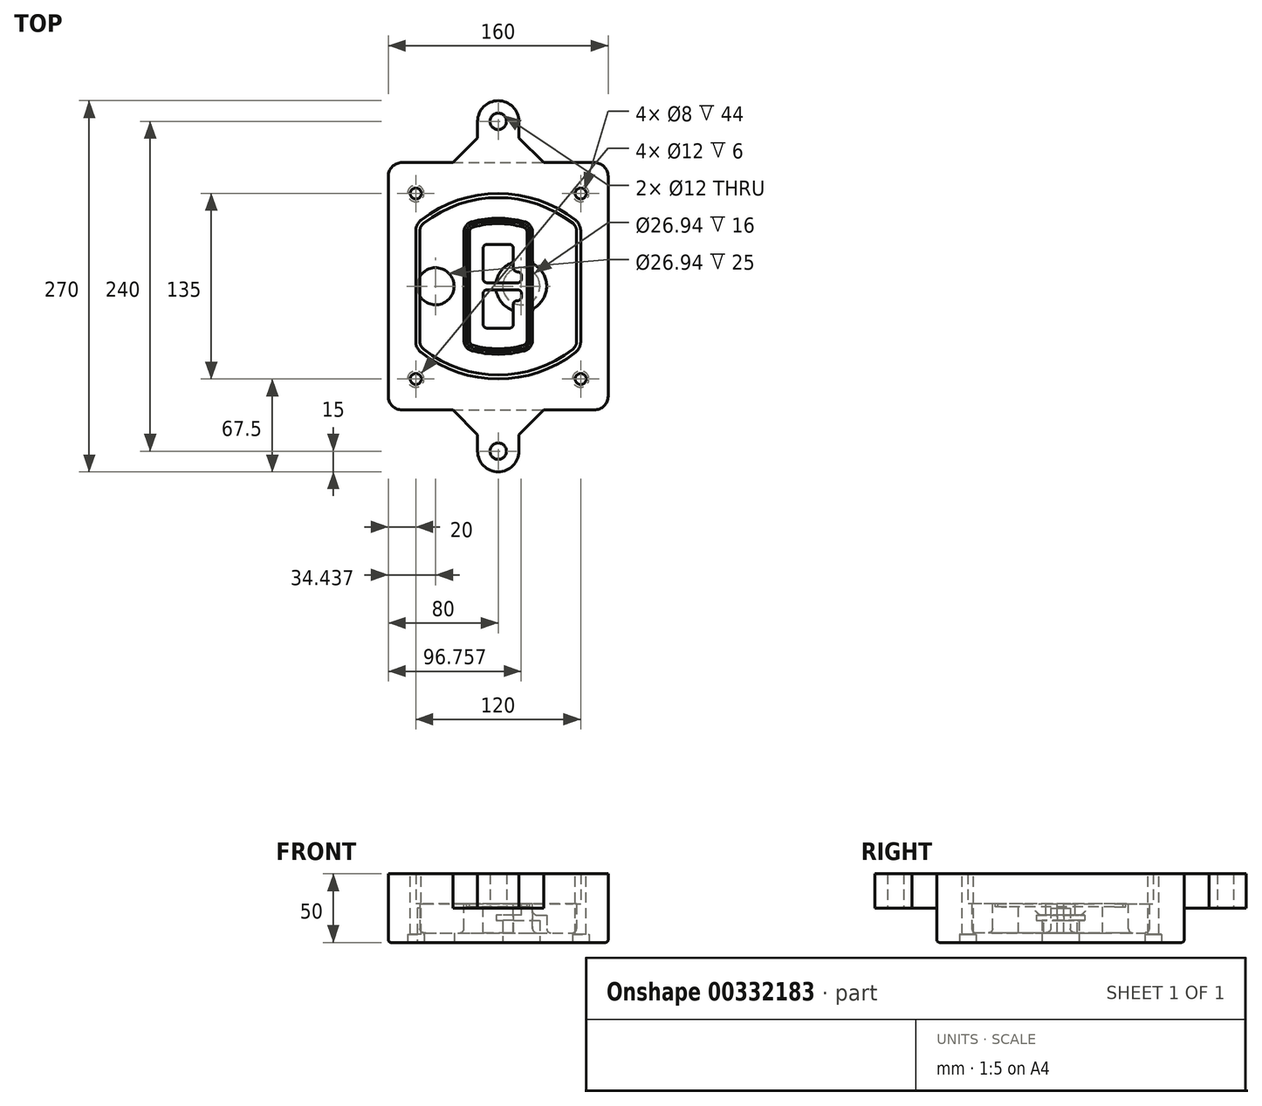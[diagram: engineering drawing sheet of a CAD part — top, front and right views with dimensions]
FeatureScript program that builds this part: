
annotation { "Feature Type Name" : "Feature", "Feature Type Description" : "" }
export const myFeature = defineFeature(function(context is Context, id is Id, definition is map)
    precondition{}
    {
        {
            var Q0;
            Q0=qCreatedBy(makeId("Top.planeOp"),FACE);
            var sketch = newSketch(context, id + "F0", { "sketchPlane" : qUnion([Q0])});
            skPoint(sketch, "E0.rect.middle", {"position": v(0, 0) * mm});
            skLineSegment(sketch, "E1.bottom", {"start": v(-70, -90) * mm, "end": v(70, -90) * mm});
            skLineSegment(sketch, "E1.top", {"start": v(-70, 90) * mm, "end": v(70, 90) * mm});
            skLineSegment(sketch, "E1.left", {"start": v(-80, -80) * mm, "end": v(-80, 80) * mm});
            skLineSegment(sketch, "E1.right", {"start": v(80, -80) * mm, "end": v(80, 80) * mm});
            skLineSegment(sketch, "E2", {"start": v(-80, 90) * mm, "end": v(80, -90) * mm, "construction": true});
            skLineSegment(sketch, "E3", {"start": v(80, 90) * mm, "end": v(-80, -90) * mm, "construction": true});
            skCircle(sketch, "E4", {"center": v(-60, 67.5) * mm, "radius": 4 * mm});
            skCircle(sketch, "E5", {"center": v(60, 67.5) * mm, "radius": 4 * mm});
            skCircle(sketch, "E6", {"center": v(60, -67.5) * mm, "radius": 4 * mm});
            skCircle(sketch, "E7", {"center": v(-60, -67.5) * mm, "radius": 4 * mm});
            skLineSegment(sketch, "E8", {"start": v(-60, 67.5) * mm, "end": v(60, 67.5) * mm, "construction": true});
            skLineSegment(sketch, "E9", {"start": v(60, 67.5) * mm, "end": v(60, -67.5) * mm, "construction": true});
            skLineSegment(sketch, "E10", {"start": v(60, -67.5) * mm, "end": v(-60, -67.5) * mm, "construction": true});
            skLineSegment(sketch, "E11", {"start": v(-60, -67.5) * mm, "end": v(-60, 67.5) * mm, "construction": true});
            skLineSegment(sketch, "E12", {"start": v(-60, 40.3) * mm, "end": v(-60, -40.3) * mm});
            skLineSegment(sketch, "E13", {"start": v(60, 40.3) * mm, "end": v(60, -40.3) * mm});
            skArc(sketch, "E14", {"start": v(56.15, 48.18) * mm, "mid": v(0, 67.5) * mm, "end": v(-56.15, 48.18) * mm});
            skArc(sketch, "E15", {"start": v(-56.15, -48.18) * mm, "mid": v(0, -67.5) * mm, "end": v(56.15, -48.18) * mm});
            skLineSegment(sketch, "E16", {"start": v(-60, 0) * mm, "end": v(60, 0) * mm, "construction": true});
            skPoint(sketch, "E17.visualSharp", {"position": v(-60, -45) * mm});
            skArc(sketch, "E17.filletArc", {"start": v(-60, -40.3) * mm, "mid": v(-58.99, -44.68) * mm, "end": v(-56.15, -48.18) * mm});
            skPoint(sketch, "E18.visualSharp", {"position": v(-60, 45) * mm});
            skArc(sketch, "E18.filletArc", {"start": v(-56.15, 48.18) * mm, "mid": v(-58.99, 44.68) * mm, "end": v(-60, 40.3) * mm});
            skPoint(sketch, "E19.visualSharp", {"position": v(60, 45) * mm});
            skArc(sketch, "E19.filletArc", {"start": v(60, 40.3) * mm, "mid": v(58.99, 44.68) * mm, "end": v(56.15, 48.18) * mm});
            skPoint(sketch, "E20.visualSharp", {"position": v(60, -45) * mm});
            skArc(sketch, "E20.filletArc", {"start": v(56.15, -48.18) * mm, "mid": v(58.99, -44.68) * mm, "end": v(60, -40.3) * mm});
            skPoint(sketch, "E21.visualSharp", {"position": v(-80, 90) * mm});
            skArc(sketch, "E21.filletArc", {"start": v(-70, 90) * mm, "mid": v(-77.07, 87.07) * mm, "end": v(-80, 80) * mm});
            skPoint(sketch, "E22.visualSharp", {"position": v(80, 90) * mm});
            skArc(sketch, "E22.filletArc", {"start": v(80, 80) * mm, "mid": v(77.07, 87.07) * mm, "end": v(70, 90) * mm});
            skPoint(sketch, "E23.visualSharp", {"position": v(80, -90) * mm});
            skArc(sketch, "E23.filletArc", {"start": v(70, -90) * mm, "mid": v(77.07, -87.07) * mm, "end": v(80, -80) * mm});
            skPoint(sketch, "E24.visualSharp", {"position": v(-80, -90) * mm});
            skArc(sketch, "E24.filletArc", {"start": v(-80, -80) * mm, "mid": v(-77.07, -87.07) * mm, "end": v(-70, -90) * mm});
            skArc(sketch, "E25.0", {"start": v(57, 40.3) * mm, "mid": v(56.3, 43.36) * mm, "end": v(54.3, 45.81) * mm});
            skLineSegment(sketch, "E25.1", {"start": v(57, 40.3) * mm, "end": v(57, -40.3) * mm});
            skArc(sketch, "E25.2", {"start": v(54.3, -45.81) * mm, "mid": v(56.3, -43.36) * mm, "end": v(57, -40.3) * mm});
            skArc(sketch, "E25.3", {"start": v(-54.3, -45.81) * mm, "mid": v(0, -64.5) * mm, "end": v(54.3, -45.81) * mm});
            skArc(sketch, "E25.4", {"start": v(-57, -40.3) * mm, "mid": v(-56.3, -43.36) * mm, "end": v(-54.3, -45.81) * mm});
            skArc(sketch, "E25.5", {"start": v(54.3, 45.81) * mm, "mid": v(0, 64.5) * mm, "end": v(-54.3, 45.81) * mm});
            skLineSegment(sketch, "E25.6", {"start": v(-57, 40.3) * mm, "end": v(-57, -40.3) * mm});
            skArc(sketch, "E25.7", {"start": v(-54.3, 45.81) * mm, "mid": v(-56.3, 43.36) * mm, "end": v(-57, 40.3) * mm});
            skArc(sketch, "E26.0", {"start": v(-58.62, 51.33) * mm, "mid": v(-62.58, 46.43) * mm, "end": v(-64, 40.3) * mm});
            skArc(sketch, "E26.1", {"start": v(58.62, 51.33) * mm, "mid": v(0, 71.5) * mm, "end": v(-58.62, 51.33) * mm});
            skArc(sketch, "E26.2", {"start": v(64, 40.3) * mm, "mid": v(62.58, 46.43) * mm, "end": v(58.62, 51.33) * mm});
            skLineSegment(sketch, "E26.3", {"start": v(64, 40.3) * mm, "end": v(64, -40.3) * mm});
            skArc(sketch, "E26.4", {"start": v(58.62, -51.33) * mm, "mid": v(62.58, -46.43) * mm, "end": v(64, -40.3) * mm});
            skLineSegment(sketch, "E26.5", {"start": v(-64, 40.3) * mm, "end": v(-64, -40.3) * mm});
            skArc(sketch, "E26.6", {"start": v(-58.62, -51.33) * mm, "mid": v(0, -71.5) * mm, "end": v(58.62, -51.33) * mm});
            skArc(sketch, "E26.7", {"start": v(-64, -40.3) * mm, "mid": v(-62.58, -46.43) * mm, "end": v(-58.62, -51.33) * mm});
            skSolve(sketch);
        }
        {
            var Q0;
            Q0=makeQuery(id+"F0.imprint","IMPRINT",FACE,{"disambiguationData":[TD([[makeQuery(id+"F0.imprint","IMPRINT",EDGE,{"derivedFrom":sQuery(id+"F0.wireOp",EDGE,"E1.bottom")}),1.0]])]});
            var Q1;
            Q1=makeQuery(id+"F0.imprint","IMPRINT",FACE,{"disambiguationData":[TD([[makeQuery(id+"F0.imprint","IMPRINT",EDGE,{"derivedFrom":sQuery(id+"F0.wireOp",EDGE,"E12")}),1.0]])]});
            var Q2;
            Q2=makeQuery(id+"F0.imprint","IMPRINT",FACE,{"disambiguationData":[TD([[makeQuery(id+"F0.imprint","IMPRINT",EDGE,{"derivedFrom":sQuery(id+"F0.wireOp",EDGE,"E25.0")}),1.0]])]});
            var Q3;
            Q3=makeQuery(id+"F0.imprint","IMPRINT",FACE,{"disambiguationData":[TD([[makeQuery(id+"F0.imprint","IMPRINT",EDGE,{"derivedFrom":sQuery(id+"F0.wireOp",EDGE,"E12")}),-1.0]])]});
            extrude(context, id + "F1", {"entities" : qUnion([Q0, Q1, Q2, Q3]), "oppositeDirection" : true, "depth" : 25 * mm});
        }
        {
            var Q0;
            Q0=makeQuery(id+"F0.imprint","IMPRINT",FACE,{"disambiguationData":[TD([[makeQuery(id+"F0.imprint","IMPRINT",EDGE,{"derivedFrom":sQuery(id+"F0.wireOp",EDGE,"E12")}),1.0]])]});
            extrude(context, id + "F2", {"entities" : qUnion([Q0]), "operationType" : NewBodyOperationType.ADD, "depth" : 3 * mm});
        }
        {
            var Q0;
            Q0=makeQuery(id+"F0.imprint","IMPRINT",FACE,{"disambiguationData":[TD([[makeQuery(id+"F0.imprint","IMPRINT",EDGE,{"derivedFrom":sQuery(id+"F0.wireOp",EDGE,"E25.0")}),1.0]])]});
            extrude(context, id + "F3", {"entities" : qUnion([Q0]), "operationType" : NewBodyOperationType.REMOVE, "oppositeDirection" : true, "depth" : 18 * mm});
        }
        {
            var Q0;
            Q0=makeQuery(id+"F2.opExtrude","CAP_FACE",FACE,{"disambiguationData":[OSD([sQuery(id+"F0.wireOp",EDGE,"E12"),sQuery(id+"F0.wireOp",EDGE,"E13"),sQuery(id+"F0.wireOp",EDGE,"E14"),sQuery(id+"F0.wireOp",EDGE,"E15"),sQuery(id+"F0.wireOp",EDGE,"E17.filletArc"),sQuery(id+"F0.wireOp",EDGE,"E18.filletArc"),sQuery(id+"F0.wireOp",EDGE,"E19.filletArc"),sQuery(id+"F0.wireOp",EDGE,"E20.filletArc"),sQuery(id+"F0.wireOp",EDGE,"E25.0"),sQuery(id+"F0.wireOp",EDGE,"E25.1"),sQuery(id+"F0.wireOp",EDGE,"E25.2"),sQuery(id+"F0.wireOp",EDGE,"E25.3"),sQuery(id+"F0.wireOp",EDGE,"E25.4"),sQuery(id+"F0.wireOp",EDGE,"E25.5"),sQuery(id+"F0.wireOp",EDGE,"E25.6"),sQuery(id+"F0.wireOp",EDGE,"E25.7")])],"isStart":false});
            var sketch = newSketch(context, id + "F4", { "sketchPlane" : qUnion([Q0])});
            skArc(sketch, "E27.0", {"start": v(-19.08, -46.97) * mm, "mid": v(0, -49.5) * mm, "end": v(19.08, -46.97) * mm});
            skArc(sketch, "E28.0", {"start": v(19.08, 46.97) * mm, "mid": v(0, 49.5) * mm, "end": v(-19.08, 46.97) * mm});
            skLineSegment(sketch, "E29", {"start": v(-25, 39.25) * mm, "end": v(-25, -39.25) * mm});
            skLineSegment(sketch, "E30", {"start": v(25, 39.25) * mm, "end": v(25, -39.25) * mm});
            skLineSegment(sketch, "E31", {"start": v(-25, 45.1) * mm, "end": v(25, 45.1) * mm, "construction": true});
            skLineSegment(sketch, "E32", {"start": v(-25, -45.1) * mm, "end": v(25, -45.1) * mm, "construction": true});
            skPoint(sketch, "E33.visualSharp", {"position": v(-25, 45.1) * mm});
            skArc(sketch, "E33.filletArc", {"start": v(-19.08, 46.97) * mm, "mid": v(-23.35, 44.11) * mm, "end": v(-25, 39.25) * mm});
            skPoint(sketch, "E34.visualSharp", {"position": v(25, 45.1) * mm});
            skArc(sketch, "E34.filletArc", {"start": v(25, 39.25) * mm, "mid": v(23.35, 44.11) * mm, "end": v(19.08, 46.97) * mm});
            skPoint(sketch, "E35.visualSharp", {"position": v(25, -45.1) * mm});
            skArc(sketch, "E35.filletArc", {"start": v(19.08, -46.97) * mm, "mid": v(23.35, -44.11) * mm, "end": v(25, -39.25) * mm});
            skPoint(sketch, "E36.visualSharp", {"position": v(-25, -45.1) * mm});
            skArc(sketch, "E36.filletArc", {"start": v(-25, -39.25) * mm, "mid": v(-23.35, -44.11) * mm, "end": v(-19.08, -46.97) * mm});
            skArc(sketch, "E37.0", {"start": v(54.3, 45.81) * mm, "mid": v(0, 64.5) * mm, "end": v(-54.3, 45.81) * mm});
            skArc(sketch, "E37.1", {"start": v(-54.3, 45.81) * mm, "mid": v(-56.3, 43.36) * mm, "end": v(-57, 40.3) * mm});
            skLineSegment(sketch, "E37.2", {"start": v(-57, 40.3) * mm, "end": v(-57, -40.3) * mm});
            skArc(sketch, "E37.3", {"start": v(-57, -40.3) * mm, "mid": v(-56.3, -43.36) * mm, "end": v(-54.3, -45.81) * mm});
            skArc(sketch, "E37.4", {"start": v(-54.3, -45.81) * mm, "mid": v(0, -64.5) * mm, "end": v(54.3, -45.81) * mm});
            skArc(sketch, "E37.5", {"start": v(54.3, -45.81) * mm, "mid": v(56.3, -43.36) * mm, "end": v(57, -40.3) * mm});
            skLineSegment(sketch, "E37.6", {"start": v(57, 40.3) * mm, "end": v(57, -40.3) * mm});
            skArc(sketch, "E37.7", {"start": v(57, 40.3) * mm, "mid": v(56.3, 43.36) * mm, "end": v(54.3, 45.81) * mm});
            skLineSegment(sketch, "E38.0", {"start": v(23, 39.25) * mm, "end": v(23, -39.25) * mm});
            skArc(sketch, "E38.1", {"start": v(18.56, -45.04) * mm, "mid": v(21.76, -42.9) * mm, "end": v(23, -39.25) * mm});
            skArc(sketch, "E38.2", {"start": v(-18.56, -45.04) * mm, "mid": v(0, -47.5) * mm, "end": v(18.56, -45.04) * mm});
            skArc(sketch, "E38.3", {"start": v(-23, -39.25) * mm, "mid": v(-21.76, -42.9) * mm, "end": v(-18.56, -45.04) * mm});
            skLineSegment(sketch, "E38.4", {"start": v(-23, 39.25) * mm, "end": v(-23, -39.25) * mm});
            skArc(sketch, "E38.5", {"start": v(23, 39.25) * mm, "mid": v(21.76, 42.9) * mm, "end": v(18.56, 45.04) * mm});
            skArc(sketch, "E38.6", {"start": v(-18.56, 45.04) * mm, "mid": v(-21.76, 42.9) * mm, "end": v(-23, 39.25) * mm});
            skArc(sketch, "E38.7", {"start": v(18.56, 45.04) * mm, "mid": v(0, 47.5) * mm, "end": v(-18.56, 45.04) * mm});
            skArc(sketch, "E39.0", {"start": v(21, 39.25) * mm, "mid": v(20.18, 41.68) * mm, "end": v(18.04, 43.1) * mm});
            skLineSegment(sketch, "E39.1", {"start": v(21, 39.25) * mm, "end": v(21, -39.25) * mm});
            skArc(sketch, "E39.2", {"start": v(18.04, -43.1) * mm, "mid": v(20.18, -41.68) * mm, "end": v(21, -39.25) * mm});
            skArc(sketch, "E39.3", {"start": v(-18.04, -43.1) * mm, "mid": v(0, -45.5) * mm, "end": v(18.04, -43.1) * mm});
            skArc(sketch, "E39.4", {"start": v(-21, -39.25) * mm, "mid": v(-20.18, -41.68) * mm, "end": v(-18.04, -43.1) * mm});
            skArc(sketch, "E39.5", {"start": v(18.04, 43.1) * mm, "mid": v(0, 45.5) * mm, "end": v(-18.04, 43.1) * mm});
            skLineSegment(sketch, "E39.6", {"start": v(-21, 39.25) * mm, "end": v(-21, -39.25) * mm});
            skArc(sketch, "E39.7", {"start": v(-18.04, 43.1) * mm, "mid": v(-20.18, 41.68) * mm, "end": v(-21, 39.25) * mm});
            skLineSegment(sketch, "E40", {"start": v(-25, 0) * mm, "end": v(25, 0) * mm, "construction": true});
            skLineSegment(sketch, "E41", {"start": v(-11, 5.5) * mm, "end": v(-11, 27.5) * mm});
            skLineSegment(sketch, "E42", {"start": v(-8, 30.5) * mm, "end": v(8, 30.5) * mm});
            skLineSegment(sketch, "E43", {"start": v(11, 27.5) * mm, "end": v(11, 13.5) * mm});
            skLineSegment(sketch, "E44", {"start": v(14, 10.5) * mm, "end": v(14, 10.5) * mm});
            skLineSegment(sketch, "E45", {"start": v(17, 7.5) * mm, "end": v(17, 5.5) * mm});
            skLineSegment(sketch, "E46", {"start": v(14, 2.5) * mm, "end": v(-8, 2.5) * mm});
            skPoint(sketch, "E47.visualSharp", {"position": v(-11, 30.5) * mm});
            skArc(sketch, "E47.filletArc", {"start": v(-8, 30.5) * mm, "mid": v(-10.12, 29.62) * mm, "end": v(-11, 27.5) * mm});
            skPoint(sketch, "E48.visualSharp", {"position": v(11, 30.5) * mm});
            skArc(sketch, "E48.filletArc", {"start": v(11, 27.5) * mm, "mid": v(10.12, 29.62) * mm, "end": v(8, 30.5) * mm});
            skPoint(sketch, "E49.visualSharp", {"position": v(11, 10.5) * mm});
            skArc(sketch, "E49.filletArc", {"start": v(11, 13.5) * mm, "mid": v(11.88, 11.38) * mm, "end": v(14, 10.5) * mm});
            skPoint(sketch, "E50.visualSharp", {"position": v(17, 10.5) * mm});
            skArc(sketch, "E50.filletArc", {"start": v(17, 7.5) * mm, "mid": v(16.12, 9.62) * mm, "end": v(14, 10.5) * mm});
            skPoint(sketch, "E51.visualSharp", {"position": v(17, 2.5) * mm});
            skArc(sketch, "E51.filletArc", {"start": v(14, 2.5) * mm, "mid": v(16.12, 3.38) * mm, "end": v(17, 5.5) * mm});
            skPoint(sketch, "E52.visualSharp", {"position": v(-11, 2.5) * mm});
            skArc(sketch, "E52.filletArc", {"start": v(-11, 5.5) * mm, "mid": v(-10.12, 3.38) * mm, "end": v(-8, 2.5) * mm});
            skLineSegment(sketch, "E53.0.MirrorCS", {"start": v(14, -2.5) * mm, "end": v(-8, -2.5) * mm});
            skArc(sketch, "E54.0.MirrorCS", {"start": v(-11, -5.5) * mm, "mid": v(-10.12, -3.38) * mm, "end": v(-8, -2.5) * mm});
            skLineSegment(sketch, "E55.0.MirrorCS", {"start": v(-11, -5.5) * mm, "end": v(-11, -27.5) * mm});
            skArc(sketch, "E56.0.MirrorCS", {"start": v(-8, -30.5) * mm, "mid": v(-10.12, -29.62) * mm, "end": v(-11, -27.5) * mm});
            skLineSegment(sketch, "E57.0.MirrorCS", {"start": v(-8, -30.5) * mm, "end": v(8, -30.5) * mm});
            skArc(sketch, "E58.0.MirrorCS", {"start": v(11, -27.5) * mm, "mid": v(10.12, -29.62) * mm, "end": v(8, -30.5) * mm});
            skLineSegment(sketch, "E59.0.MirrorCS", {"start": v(11, -27.5) * mm, "end": v(11, -13.5) * mm});
            skArc(sketch, "E60.0.MirrorCS", {"start": v(11, -13.5) * mm, "mid": v(11.88, -11.38) * mm, "end": v(14, -10.5) * mm});
            skArc(sketch, "E61.0.MirrorCS", {"start": v(17, -7.5) * mm, "mid": v(16.12, -9.62) * mm, "end": v(14, -10.5) * mm});
            skLineSegment(sketch, "E62.0.MirrorCS", {"start": v(17, -7.5) * mm, "end": v(17, -5.5) * mm});
            skArc(sketch, "E63.0.MirrorCS", {"start": v(14, -2.5) * mm, "mid": v(16.12, -3.38) * mm, "end": v(17, -5.5) * mm});
            skSolve(sketch);
        }
        {
            var Q0;
            Q0=makeQuery(id+"F4.imprint","IMPRINT",FACE,{"disambiguationData":[TD([[makeQuery(id+"F4.imprint","IMPRINT",EDGE,{"derivedFrom":sQuery(id+"F4.wireOp",EDGE,"E27.0")}),1.0]])]});
            var Q1;
            Q1=makeQuery(id+"F4.imprint","IMPRINT",FACE,{"disambiguationData":[TD([[makeQuery(id+"F4.imprint","IMPRINT",EDGE,{"derivedFrom":sQuery(id+"F4.wireOp",EDGE,"E38.0")}),-1.0]])]});
            var Q2;
            Q2=makeQuery(id+"F4.imprint","IMPRINT",FACE,{"disambiguationData":[TD([[makeQuery(id+"F4.imprint","IMPRINT",EDGE,{"derivedFrom":sQuery(id+"F4.wireOp",EDGE,"E39.0")}),1.0]])]});
            extrude(context, id + "F5", {"entities" : qUnion([Q0, Q1, Q2]), "operationType" : NewBodyOperationType.ADD, "endBound" : BoundingType.UP_TO_NEXT, "oppositeDirection" : true, "depth" : 25 * mm});
        }
        {
            var Q0;
            Q0=makeQuery(id+"F4.imprint","IMPRINT",FACE,{"disambiguationData":[TD([[makeQuery(id+"F4.imprint","IMPRINT",EDGE,{"derivedFrom":sQuery(id+"F4.wireOp",EDGE,"E38.0")}),-1.0]])]});
            extrude(context, id + "F6", {"entities" : qUnion([Q0]), "operationType" : NewBodyOperationType.REMOVE, "oppositeDirection" : true, "depth" : 2 * mm});
        }
        {
            var Q0;
            Q0=makeQuery(id+"F1.opExtrude","CAP_FACE",FACE,{"disambiguationData":[OSD([sQuery(id+"F0.wireOp",EDGE,"E1.bottom"),sQuery(id+"F0.wireOp",EDGE,"E1.top"),sQuery(id+"F0.wireOp",EDGE,"E1.left"),sQuery(id+"F0.wireOp",EDGE,"E1.right"),sQuery(id+"F0.wireOp",EDGE,"E4"),sQuery(id+"F0.wireOp",EDGE,"E5"),sQuery(id+"F0.wireOp",EDGE,"E6"),sQuery(id+"F0.wireOp",EDGE,"E7"),sQuery(id+"F0.wireOp",EDGE,"E21.filletArc"),sQuery(id+"F0.wireOp",EDGE,"E22.filletArc"),sQuery(id+"F0.wireOp",EDGE,"E23.filletArc"),sQuery(id+"F0.wireOp",EDGE,"E24.filletArc")])],"isStart":false});
            var sketch = newSketch(context, id + "F7", { "sketchPlane" : qUnion([Q0])});
            skCircle(sketch, "E64", {"center": v(16.76, 0) * mm, "radius": 13.47 * mm});
            skCircle(sketch, "E65", {"center": v(-45.56, 0) * mm, "radius": 13.47 * mm});
            skLineSegment(sketch, "E66", {"start": v(80, 0) * mm, "end": v(-80, 0) * mm});
            skCircle(sketch, "E67", {"center": v(16.76, 0) * mm, "radius": 18.47 * mm});
            skCircle(sketch, "E68", {"center": v(60, -67.5) * mm, "radius": 6 * mm});
            skCircle(sketch, "E69", {"center": v(-60, -67.5) * mm, "radius": 6 * mm});
            skCircle(sketch, "E70", {"center": v(-60, 67.5) * mm, "radius": 6 * mm});
            skCircle(sketch, "E71", {"center": v(60, 67.5) * mm, "radius": 6 * mm});
            skSolve(sketch);
        }
        {
            var Q0;
            {var subQ1=sQuery(id+"F7.wireOp",EDGE,"E66");var subQ4=sQuery(id+"F7.wireOp",EDGE,"E64");var subQ6=makeQuery(id+"F7.imprint","INTERSECT",VERTEX,{"disambiguationData":[OD(0.0)],"derivedFrom":[subQ4,subQ1]});Q0=makeQuery(id+"F7.imprint","IMPRINT",FACE,{"disambiguationData":[TD([[makeQuery(id+"F7.imprint","IMPRINT",EDGE,{"disambiguationData":[TD([[subQ6,-1.0]])],"derivedFrom":subQ4}),-1.0]])]});}
            var Q1;
            {var subQ0=sQuery(id+"F7.wireOp",EDGE,"E66");var subQ1=sQuery(id+"F7.wireOp",EDGE,"E64");var subQ3=makeQuery(id+"F7.imprint","INTERSECT",VERTEX,{"disambiguationData":[OD(0.0)],"derivedFrom":[subQ1,subQ0]});Q1=makeQuery(id+"F7.imprint","IMPRINT",FACE,{"disambiguationData":[TD([[makeQuery(id+"F7.imprint","IMPRINT",EDGE,{"disambiguationData":[TD([[subQ3,-1.0]])],"derivedFrom":subQ1}),1.0]])]});}
            var Q2;
            {var subQ0=sQuery(id+"F7.wireOp",EDGE,"E66");var subQ1=sQuery(id+"F7.wireOp",EDGE,"E64");var subQ3=makeQuery(id+"F7.imprint","INTERSECT",VERTEX,{"disambiguationData":[OD(0.0)],"derivedFrom":[subQ1,subQ0]});Q2=makeQuery(id+"F7.imprint","IMPRINT",FACE,{"disambiguationData":[TD([[makeQuery(id+"F7.imprint","IMPRINT",EDGE,{"disambiguationData":[TD([[subQ3,1.0]])],"derivedFrom":subQ1}),1.0]])]});}
            var Q3;
            {var subQ1=sQuery(id+"F7.wireOp",EDGE,"E66");var subQ4=sQuery(id+"F7.wireOp",EDGE,"E64");var subQ6=makeQuery(id+"F7.imprint","INTERSECT",VERTEX,{"disambiguationData":[OD(0.0)],"derivedFrom":[subQ4,subQ1]});Q3=makeQuery(id+"F7.imprint","IMPRINT",FACE,{"disambiguationData":[TD([[makeQuery(id+"F7.imprint","IMPRINT",EDGE,{"disambiguationData":[TD([[subQ6,1.0]])],"derivedFrom":subQ4}),-1.0]])]});}
            extrude(context, id + "F8", {"entities" : qUnion([Q0, Q1, Q2, Q3]), "operationType" : NewBodyOperationType.ADD, "oppositeDirection" : true, "depth" : 20 * mm});
        }
        {
            var Q0;
            {var subQ0=sQuery(id+"F7.wireOp",EDGE,"E66");var subQ1=sQuery(id+"F7.wireOp",EDGE,"E64");var subQ3=makeQuery(id+"F7.imprint","INTERSECT",VERTEX,{"disambiguationData":[OD(0.0)],"derivedFrom":[subQ1,subQ0]});Q0=makeQuery(id+"F7.imprint","IMPRINT",FACE,{"disambiguationData":[TD([[makeQuery(id+"F7.imprint","IMPRINT",EDGE,{"disambiguationData":[TD([[subQ3,-1.0]])],"derivedFrom":subQ1}),1.0]])]});}
            var Q1;
            {var subQ0=sQuery(id+"F7.wireOp",EDGE,"E66");var subQ1=sQuery(id+"F7.wireOp",EDGE,"E64");var subQ3=makeQuery(id+"F7.imprint","INTERSECT",VERTEX,{"disambiguationData":[OD(0.0)],"derivedFrom":[subQ1,subQ0]});Q1=makeQuery(id+"F7.imprint","IMPRINT",FACE,{"disambiguationData":[TD([[makeQuery(id+"F7.imprint","IMPRINT",EDGE,{"disambiguationData":[TD([[subQ3,1.0]])],"derivedFrom":subQ1}),1.0]])]});}
            extrude(context, id + "F9", {"entities" : qUnion([Q0, Q1]), "operationType" : NewBodyOperationType.REMOVE, "oppositeDirection" : true, "depth" : 16 * mm});
        }
        {
            var Q0;
            {var subQ0=sQuery(id+"F7.wireOp",EDGE,"E66");var subQ1=sQuery(id+"F7.wireOp",EDGE,"E65");var subQ3=makeQuery(id+"F7.imprint","INTERSECT",VERTEX,{"disambiguationData":[OD(0.0)],"derivedFrom":[subQ1,subQ0]});Q0=makeQuery(id+"F7.imprint","IMPRINT",FACE,{"disambiguationData":[TD([[makeQuery(id+"F7.imprint","IMPRINT",EDGE,{"disambiguationData":[TD([[subQ3,-1.0]])],"derivedFrom":subQ1}),1.0]])]});}
            var Q1;
            {var subQ0=sQuery(id+"F7.wireOp",EDGE,"E66");var subQ1=sQuery(id+"F7.wireOp",EDGE,"E65");var subQ3=makeQuery(id+"F7.imprint","INTERSECT",VERTEX,{"disambiguationData":[OD(0.0)],"derivedFrom":[subQ1,subQ0]});Q1=makeQuery(id+"F7.imprint","IMPRINT",FACE,{"disambiguationData":[TD([[makeQuery(id+"F7.imprint","IMPRINT",EDGE,{"disambiguationData":[TD([[subQ3,1.0]])],"derivedFrom":subQ1}),1.0]])]});}
            extrude(context, id + "F10", {"entities" : qUnion([Q0, Q1]), "operationType" : NewBodyOperationType.REMOVE, "oppositeDirection" : true, "depth" : 25 * mm});
        }
        {
            var Q0;
            Q0=makeQuery(id+"F7.imprint","IMPRINT",FACE,{"disambiguationData":[TD([[makeQuery(id+"F7.imprint","IMPRINT",EDGE,{"derivedFrom":sQuery(id+"F7.wireOp",EDGE,"E68")}),1.0]])]});
            var Q1;
            Q1=makeQuery(id+"F7.imprint","IMPRINT",FACE,{"disambiguationData":[TD([[makeQuery(id+"F7.imprint","IMPRINT",EDGE,{"derivedFrom":makeQuery(id+"F1.opExtrude","CAP_EDGE",EDGE,{"disambiguationData":[OSD([sQuery(id+"F0.wireOp",EDGE,"E5")])],"isStart":false})}),-1.0]])]});
            var Q2;
            Q2=makeQuery(id+"F7.imprint","IMPRINT",FACE,{"disambiguationData":[TD([[makeQuery(id+"F7.imprint","IMPRINT",EDGE,{"derivedFrom":sQuery(id+"F7.wireOp",EDGE,"E69")}),1.0]])]});
            var Q3;
            Q3=makeQuery(id+"F7.imprint","IMPRINT",FACE,{"disambiguationData":[TD([[makeQuery(id+"F7.imprint","IMPRINT",EDGE,{"derivedFrom":makeQuery(id+"F1.opExtrude","CAP_EDGE",EDGE,{"disambiguationData":[OSD([sQuery(id+"F0.wireOp",EDGE,"E4")])],"isStart":false})}),-1.0]])]});
            var Q4;
            Q4=makeQuery(id+"F7.imprint","IMPRINT",FACE,{"disambiguationData":[TD([[makeQuery(id+"F7.imprint","IMPRINT",EDGE,{"derivedFrom":sQuery(id+"F7.wireOp",EDGE,"E70")}),1.0]])]});
            var Q5;
            Q5=makeQuery(id+"F7.imprint","IMPRINT",FACE,{"disambiguationData":[TD([[makeQuery(id+"F7.imprint","IMPRINT",EDGE,{"derivedFrom":makeQuery(id+"F1.opExtrude","CAP_EDGE",EDGE,{"disambiguationData":[OSD([sQuery(id+"F0.wireOp",EDGE,"E7")])],"isStart":false})}),-1.0]])]});
            var Q6;
            Q6=makeQuery(id+"F7.imprint","IMPRINT",FACE,{"disambiguationData":[TD([[makeQuery(id+"F7.imprint","IMPRINT",EDGE,{"derivedFrom":sQuery(id+"F7.wireOp",EDGE,"E71")}),1.0]])]});
            var Q7;
            Q7=makeQuery(id+"F7.imprint","IMPRINT",FACE,{"disambiguationData":[TD([[makeQuery(id+"F7.imprint","IMPRINT",EDGE,{"derivedFrom":makeQuery(id+"F1.opExtrude","CAP_EDGE",EDGE,{"disambiguationData":[OSD([sQuery(id+"F0.wireOp",EDGE,"E6")])],"isStart":false})}),-1.0]])]});
            extrude(context, id + "F11", {"entities" : qUnion([Q0, Q1, Q2, Q3, Q4, Q5, Q6, Q7]), "operationType" : NewBodyOperationType.REMOVE, "oppositeDirection" : true, "depth" : 6 * mm});
        }
        {
            var Q0;
            Q0=makeQuery(id+"F9.boolean.opBoolean","COPY",FACE,{"derivedFrom":makeQuery(id+"F9.opExtrude","CAP_FACE",FACE,{"disambiguationData":[OSD([sQuery(id+"F7.wireOp",EDGE,"E64")])],"isStart":false})});
            var sketch = newSketch(context, id + "F12", { "sketchPlane" : qUnion([Q0])});
            skArc(sketch, "E72.0", {"start": v(11, 17.55) * mm, "mid": v(2.57, 11.82) * mm, "end": v(-1.54, 2.5) * mm});
            skArc(sketch, "E72.1", {"start": v(-1.54, -2.5) * mm, "mid": v(2.57, -11.82) * mm, "end": v(11, -17.55) * mm});
            skLineSegment(sketch, "E73", {"start": v(-1.54, -2.5) * mm, "end": v(14, -2.5) * mm});
            skLineSegment(sketch, "E74.0", {"start": v(14, 2.5) * mm, "end": v(-1.54, 2.5) * mm});
            skArc(sketch, "E74.1", {"start": v(14, 2.5) * mm, "mid": v(16.12, 3.38) * mm, "end": v(17, 5.5) * mm});
            skLineSegment(sketch, "E74.2", {"start": v(17, 7.5) * mm, "end": v(17, 5.5) * mm});
            skArc(sketch, "E74.3", {"start": v(17, 7.5) * mm, "mid": v(16.12, 9.62) * mm, "end": v(14, 10.5) * mm});
            skArc(sketch, "E74.4", {"start": v(11, 13.5) * mm, "mid": v(11.88, 11.38) * mm, "end": v(14, 10.5) * mm});
            skLineSegment(sketch, "E74.5", {"start": v(11, 17.55) * mm, "end": v(11, 13.5) * mm});
            skLineSegment(sketch, "E74.7", {"start": v(14, -2.5) * mm, "end": v(-1.54, -2.5) * mm});
            skArc(sketch, "E74.8", {"start": v(14, -2.5) * mm, "mid": v(16.12, -3.38) * mm, "end": v(17, -5.5) * mm});
            skLineSegment(sketch, "E74.9", {"start": v(17, -7.5) * mm, "end": v(17, -5.5) * mm});
            skArc(sketch, "E74.10", {"start": v(17, -7.5) * mm, "mid": v(16.12, -9.62) * mm, "end": v(14, -10.5) * mm});
            skArc(sketch, "E74.11", {"start": v(11, -13.5) * mm, "mid": v(11.88, -11.38) * mm, "end": v(14, -10.5) * mm});
            skLineSegment(sketch, "E74.12", {"start": v(11, -17.55) * mm, "end": v(11, -13.5) * mm});
            skPoint(sketch, "E75.orphan", {"position": v(11, -27.5) * mm});
            skPoint(sketch, "E76.orphan", {"position": v(-8, -2.5) * mm});
            skPoint(sketch, "E77.orphan", {"position": v(-8, 2.5) * mm});
            skPoint(sketch, "E78.orphan", {"position": v(11, 27.5) * mm});
            skSolve(sketch);
        }
        {
            var Q0;
            {var subQ7=sQuery(id+"F12.wireOp",EDGE,"E72.0");var subQ14=sQuery(id+"F12.wireOp",EDGE,"E72.1");var subQ16=sQuery(id+"F12.wireOp",EDGE,"E74.1");var subQ18=sQuery(id+"F12.wireOp",EDGE,"E74.8");Q0=qUnion([makeQuery(id+"F12.imprint","IMPRINT",FACE,{"disambiguationData":[TD([[makeQuery(id+"F12.imprint","IMPRINT",EDGE,{"derivedFrom":subQ7}),1.0]])]}),makeQuery(id+"F12.imprint","IMPRINT",FACE,{"disambiguationData":[TD([[makeQuery(id+"F12.imprint","IMPRINT",EDGE,{"derivedFrom":subQ14}),1.0]])]}),makeQuery(id+"F12.imprint","IMPRINT",FACE,{"disambiguationData":[TD([[makeQuery(id+"F12.imprint","IMPRINT",EDGE,{"derivedFrom":subQ16}),1.0]])]}),makeQuery(id+"F12.imprint","IMPRINT",FACE,{"disambiguationData":[TD([[makeQuery(id+"F12.imprint","IMPRINT",EDGE,{"derivedFrom":subQ18}),-1.0]])]})]);}
            var Q1;
            Q1=makeQuery(id+"F5.boolean.opBoolean","SPLIT",FACE,{"disambiguationData":[TD([makeQuery(id+"F5.opExtrude","SWEPT_FACE",FACE,{"disambiguationData":[OSD([sQuery(id+"F4.wireOp",EDGE,"E41")])]})])],"derivedFrom":makeQuery(id+"F3.boolean.opBoolean","COPY",FACE,{"derivedFrom":makeQuery(id+"F3.opExtrude","CAP_FACE",FACE,{"disambiguationData":[OSD([sQuery(id+"F0.wireOp",EDGE,"E25.0"),sQuery(id+"F0.wireOp",EDGE,"E25.1"),sQuery(id+"F0.wireOp",EDGE,"E25.2"),sQuery(id+"F0.wireOp",EDGE,"E25.3"),sQuery(id+"F0.wireOp",EDGE,"E25.4"),sQuery(id+"F0.wireOp",EDGE,"E25.5"),sQuery(id+"F0.wireOp",EDGE,"E25.6"),sQuery(id+"F0.wireOp",EDGE,"E25.7")])],"isStart":false})})});
            extrude(context, id + "F13", {"entities" : qUnion([Q0]), "operationType" : NewBodyOperationType.REMOVE, "endBound" : BoundingType.UP_TO_SURFACE, "endBoundEntityFace" : qUnion([Q1]), "depth" : 25 * mm});
        }
        {
            var Q0;
            Q0=makeQuery(id+"F3.boolean.opBoolean","COPY",EDGE,{"derivedFrom":makeQuery(id+"F3.opExtrude","CAP_EDGE",EDGE,{"disambiguationData":[OSD([sQuery(id+"F0.wireOp",EDGE,"E25.6")])],"isStart":false})});
            var Q1;
            Q1=makeQuery(id+"F8.boolean.opBoolean","INTERSECT",EDGE,{"derivedFrom":[makeQuery(id+"F5.opExtrude","SWEPT_FACE",FACE,{"disambiguationData":[OSD([sQuery(id+"F4.wireOp",EDGE,"E30")])]}),makeQuery(id+"F8.opExtrude","CAP_FACE",FACE,{"disambiguationData":[OSD([sQuery(id+"F7.wireOp",EDGE,"E67")])],"isStart":false})]});
            var Q2;
            Q2=makeQuery(id+"F8.boolean.opBoolean","INTERSECT",EDGE,{"disambiguationData":[OD(1.0)],"derivedFrom":[makeQuery(id+"F5.opExtrude","SWEPT_FACE",FACE,{"disambiguationData":[OSD([sQuery(id+"F4.wireOp",EDGE,"E30")])]}),makeQuery(id+"F8.opExtrude","SWEPT_FACE",FACE,{"disambiguationData":[OSD([sQuery(id+"F7.wireOp",EDGE,"E67")])]})]});
            var Q3;
            {var subQ0=sQuery(id+"F4.wireOp",EDGE,"E30");Q3=makeQuery(id+"F8.boolean.opBoolean","SPLIT",EDGE,{"disambiguationData":[TD([makeQuery(id+"F5.opExtrude","SWEPT_FACE",FACE,{"disambiguationData":[OSD([sQuery(id+"F4.wireOp",EDGE,"E35.filletArc")])]})])],"derivedFrom":makeQuery(id+"F5.opExtrude","CAP_EDGE",EDGE,{"disambiguationData":[OSD([subQ0])],"isStart":false})});}
            var Q4;
            {var subQ0=sQuery(id+"F0.wireOp",EDGE,"E25.7");var subQ1=sQuery(id+"F0.wireOp",EDGE,"E25.1");var subQ2=sQuery(id+"F0.wireOp",EDGE,"E25.6");var subQ3=sQuery(id+"F0.wireOp",EDGE,"E25.5");var subQ4=sQuery(id+"F0.wireOp",EDGE,"E25.4");var subQ5=sQuery(id+"F0.wireOp",EDGE,"E25.0");var subQ6=sQuery(id+"F0.wireOp",EDGE,"E25.2");var subQ7=sQuery(id+"F0.wireOp",EDGE,"E25.3");Q4=makeQuery(id+"F8.boolean.opBoolean","INTERSECT",EDGE,{"derivedFrom":[makeQuery(id+"F5.boolean.opBoolean","SPLIT",FACE,{"disambiguationData":[TD([makeQuery(id+"F2.opExtrude","SWEPT_FACE",FACE,{"disambiguationData":[OSD([subQ5])]})])],"derivedFrom":makeQuery(id+"F3.boolean.opBoolean","COPY",FACE,{"derivedFrom":makeQuery(id+"F3.opExtrude","CAP_FACE",FACE,{"disambiguationData":[OSD([subQ5,subQ1,subQ6,subQ7,subQ4,subQ3,subQ2,subQ0])],"isStart":false})})}),makeQuery(id+"F8.opExtrude","SWEPT_FACE",FACE,{"disambiguationData":[OSD([sQuery(id+"F7.wireOp",EDGE,"E67")])]})]});}
            var Q5;
            Q5=makeQuery(id+"F8.boolean.opBoolean","INTERSECT",EDGE,{"disambiguationData":[OD(0.0)],"derivedFrom":[makeQuery(id+"F5.opExtrude","SWEPT_FACE",FACE,{"disambiguationData":[OSD([sQuery(id+"F4.wireOp",EDGE,"E30")])]}),makeQuery(id+"F8.opExtrude","SWEPT_FACE",FACE,{"disambiguationData":[OSD([sQuery(id+"F7.wireOp",EDGE,"E67")])]})]});
            fillet(context, id + "F14", {"entities" : qUnion([Q0, Q1, Q2, Q3, Q4, Q5]), "radius" : 3 * mm, "tangentPropagation" : true, "allowEdgeOverflow" : false});
        }
        {
            var Q0;
            Q0=makeQuery(id+"F1.opExtrude","CAP_EDGE",EDGE,{"disambiguationData":[OSD([sQuery(id+"F0.wireOp",EDGE,"E1.bottom")])],"isStart":false});
            fillet(context, id + "F15", {"entities" : qUnion([Q0]), "radius" : 2 * mm, "tangentPropagation" : true, "allowEdgeOverflow" : false});
        }
        {
            var Q0;
            {var subQ0=sQuery(id+"F0.wireOp",EDGE,"E21.filletArc");var subQ1=sQuery(id+"F0.wireOp",EDGE,"E7");var subQ2=sQuery(id+"F0.wireOp",EDGE,"E6");var subQ3=sQuery(id+"F0.wireOp",EDGE,"E5");var subQ4=sQuery(id+"F0.wireOp",EDGE,"E4");var subQ5=sQuery(id+"F0.wireOp",EDGE,"E22.filletArc");var subQ6=sQuery(id+"F0.wireOp",EDGE,"E1.bottom");var subQ7=sQuery(id+"F0.wireOp",EDGE,"E1.right");var subQ8=sQuery(id+"F0.wireOp",EDGE,"E1.top");var subQ9=sQuery(id+"F0.wireOp",EDGE,"E1.left");var subQ10=sQuery(id+"F0.wireOp",EDGE,"E23.filletArc");var subQ11=sQuery(id+"F0.wireOp",EDGE,"E24.filletArc");Q0=makeQuery(id+"F2.boolean.opBoolean","SPLIT",FACE,{"disambiguationData":[TD([makeQuery(id+"F1.opExtrude","SWEPT_FACE",FACE,{"disambiguationData":[OSD([subQ6])]})])],"derivedFrom":makeQuery(id+"F1.opExtrude","CAP_FACE",FACE,{"disambiguationData":[OSD([subQ6,subQ8,subQ9,subQ7,subQ4,subQ3,subQ2,subQ1,subQ0,subQ5,subQ10,subQ11])],"isStart":true})});}
            var sketch = newSketch(context, id + "F16", { "sketchPlane" : qUnion([Q0])});
            skLineSegment(sketch, "E79", {"start": v(0, 90) * mm, "end": v(0, 120) * mm, "construction": true});
            skCircle(sketch, "E80", {"center": v(0, 120) * mm, "radius": 6 * mm});
            skLineSegment(sketch, "E81", {"start": v(-33, 90) * mm, "end": v(-15, 108) * mm});
            skLineSegment(sketch, "E82", {"start": v(-15, 108) * mm, "end": v(-15, 120) * mm});
            skPoint(sketch, "E83.endSnap0", {"position": v(0, 105) * mm});
            skArc(sketch, "E84", {"start": v(15, 120) * mm, "mid": v(0, 135) * mm, "end": v(-15, 120) * mm});
            skLineSegment(sketch, "E85", {"start": v(15, 108) * mm, "end": v(33, 90) * mm});
            skLineSegment(sketch, "E86", {"start": v(15, 108) * mm, "end": v(15, 120) * mm});
            skLineSegment(sketch, "E87", {"start": v(-80, 0) * mm, "end": v(80, 0) * mm});
            skLineSegment(sketch, "E88", {"start": v(80, 0) * mm, "end": v(-80, 0) * mm, "construction": true});
            skLineSegment(sketch, "E89.MirrorCS", {"start": v(-33, -90) * mm, "end": v(-15, -108) * mm});
            skLineSegment(sketch, "E90.MirrorCS", {"start": v(-15, -108) * mm, "end": v(-15, -120) * mm});
            skArc(sketch, "E91.MirrorCS", {"start": v(15, -120) * mm, "mid": v(0, -135) * mm, "end": v(-15, -120) * mm});
            skLineSegment(sketch, "E92.MirrorCS", {"start": v(15, -108) * mm, "end": v(15, -120) * mm});
            skLineSegment(sketch, "E93.MirrorCS", {"start": v(15, -108) * mm, "end": v(33, -90) * mm});
            skLineSegment(sketch, "E94.MirrorCS", {"start": v(0, -90) * mm, "end": v(0, -120) * mm, "construction": true});
            skCircle(sketch, "E95.MirrorC", {"center": v(0, -120) * mm, "radius": 6 * mm});
            skSolve(sketch);
        }
        {
            var Q0;
            Q0=makeQuery(id+"F16.imprint","IMPRINT",FACE,{"disambiguationData":[TD([[makeQuery(id+"F16.imprint","IMPRINT",EDGE,{"derivedFrom":makeQuery(id+"F1.opExtrude","CAP_EDGE",EDGE,{"disambiguationData":[OSD([sQuery(id+"F0.wireOp",EDGE,"E6")])],"isStart":true})}),-1.0]])]});
            var Q1;
            Q1=makeQuery(id+"F16.imprint","IMPRINT",FACE,{"disambiguationData":[TD([[makeQuery(id+"F16.imprint","IMPRINT",EDGE,{"derivedFrom":makeQuery(id+"F1.opExtrude","CAP_EDGE",EDGE,{"disambiguationData":[OSD([sQuery(id+"F0.wireOp",EDGE,"E4")])],"isStart":true})}),-1.0]])]});
            var Q2;
            Q2=makeQuery(id+"F16.imprint","IMPRINT",FACE,{"disambiguationData":[TD([[makeQuery(id+"F16.imprint","IMPRINT",EDGE,{"derivedFrom":sQuery(id+"F16.wireOp",EDGE,"E80")}),-1.0]])]});
            var Q3;
            {var subQ0=sQuery(id+"F16.wireOp",EDGE,"E89.MirrorCS");Q3=makeQuery(id+"F16.imprint","IMPRINT",FACE,{"disambiguationData":[TD([[makeQuery(id+"F16.imprint","IMPRINT",EDGE,{"derivedFrom":subQ0}),1.0]])]});}
            extrude(context, id + "F17", {"entities" : qUnion([Q0, Q1, Q2, Q3]), "operationType" : NewBodyOperationType.ADD, "depth" : 25 * mm});
        }
    });
